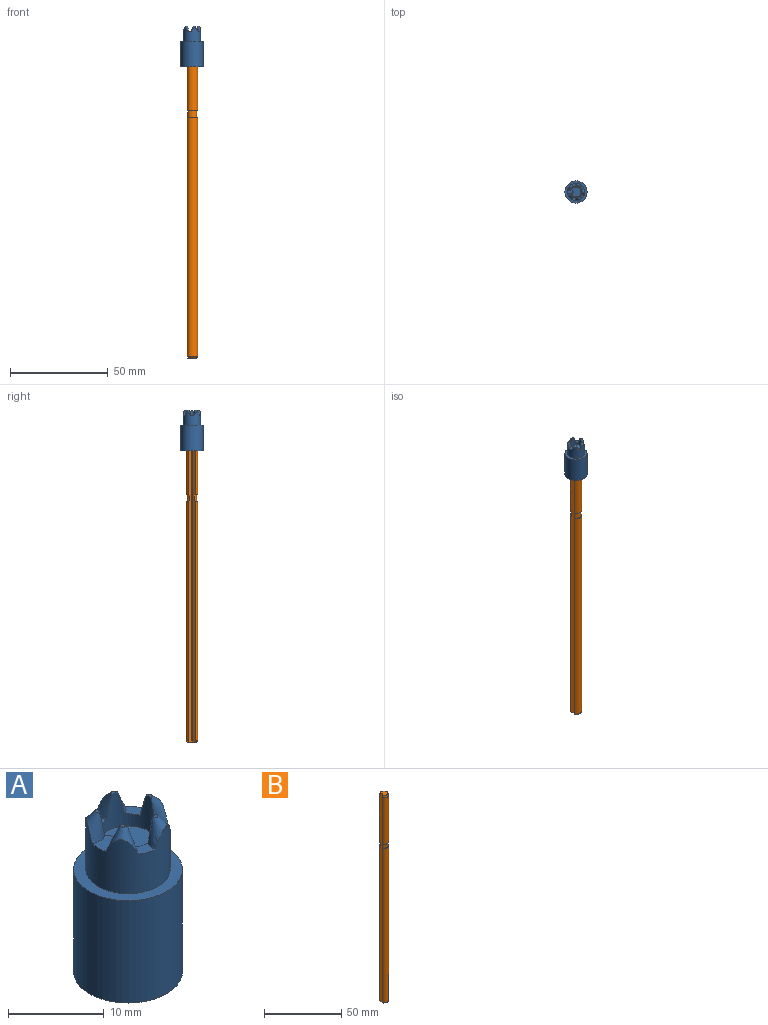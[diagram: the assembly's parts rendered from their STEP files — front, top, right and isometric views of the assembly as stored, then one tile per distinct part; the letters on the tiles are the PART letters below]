
ASSEMBLY  parts=2 mates=1
PART A: 33 faces, bbox 11.7x11.7x21.3 mm
  f0: cylinder r=3.06mm len=6.12mm, axis (0,0,-1), area 44.5mm2, adj f1,f4,f6,f7,f10,f11,f12,f13
  f1: cylinder r=0.15mm len=4.37mm, axis (0,0,-1), area 0.8mm2, adj f0,f2,f17,f32
  f2: plane 3.77x0.68mm, normal (0.71,0.71,0), area 1.9mm2, adj f1,f5,f17,f18,f32
  f3: plane 3.77x0.68mm, normal (0.71,-0.71,0), area 1.9mm2, adj f4,f5,f18,f22,f32
  f4: cylinder r=0.15mm len=4.37mm, axis (0,0,-1), area 0.8mm2, adj f0,f3,f22,f32
  f5: cylinder r=0.9mm len=1.57mm, axis (0,0,-1), area 2.2mm2, adj f2,f3,f18,f32
  f6: cone r=1.8mm half-angle=24.8deg, axis (0.34,0,-0.94), area 9mm2, adj f0,f7,f9,f10,f27
  f7: plane 0.97x0.71mm, normal (0,0,1), area 0.2mm2, adj f0,f6
  f8: cylinder r=3.06mm len=15.9mm, axis (0,0,-1), area 255.9mm2, adj f15,f21,f29,f31
  f9: cylinder r=4.4mm len=8.8mm, axis (0,0,-1), area 159.2mm2, adj f6,f10,f12,f13,f17,f18,f22,f23
  f10: plane 2.32x2.22mm, normal (0,0,1), area 2.2mm2, adj f0,f6,f9,f12
  f11: plane 0.97x0.81mm, normal (0,0,1), area 0.2mm2, adj f0,f12
  f12: cone r=1.8mm half-angle=24.8deg, axis (0.11,0.33,-0.94), area 9mm2, adj f0,f9,f10,f11,f13
  f13: plane 2.2x1.91mm, normal (0,0,1), area 2.2mm2, adj f0,f9,f12,f17
  f14: plane 0.63x0.58mm, normal (0,0,1), area 0.2mm2, adj f0,f17
  f15: cylinder r=0.15mm len=15.9mm, axis (0,0,-1), area 3.1mm2, adj f8,f16,f29,f31
  f16: plane 15.9x0.68mm, normal (0.71,0.71,0), area 15.3mm2, adj f15,f26,f29,f31
  f17: cone r=1.8mm half-angle=24.8deg, axis (-0.28,0.2,-0.94), area 9.8mm2, adj f0,f1,f2,f9,f13,f14,f18
  f18: plane 2.7x2.17mm, normal (0,0,1), area 4.4mm2, adj f2,f3,f5,f9,f17,f22
  f19: plane 0.63x0.58mm, normal (0,0,1), area 0.2mm2, adj f0,f22
  f20: plane 15.9x0.68mm, normal (0.71,-0.71,0), area 15.3mm2, adj f21,f26,f29,f31
  f21: cylinder r=0.15mm len=15.9mm, axis (0,0,-1), area 3.1mm2, adj f8,f20,f29,f31
  f22: cone r=1.8mm half-angle=24.8deg, axis (-0.28,-0.2,-0.94), area 9.8mm2, adj f0,f3,f4,f9,f18,f19,f23
  f23: plane 2.2x1.91mm, normal (0,0,1), area 2.2mm2, adj f0,f9,f22,f24
  f24: cone r=1.8mm half-angle=24.8deg, axis (0.11,-0.33,-0.94), area 9mm2, adj f0,f9,f23,f25,f27
  f25: plane 0.97x0.81mm, normal (0,0,1), area 0.2mm2, adj f0,f24
  f26: cylinder r=0.9mm len=15.9mm, axis (0,0,-1), area 22.5mm2, adj f16,f20,f29,f31
  f27: plane 2.32x2.22mm, normal (0,0,1), area 2.2mm2, adj f0,f6,f9,f24
  f28: cylinder r=5.68mm len=13.05mm, axis (0,0,1), area 465.3mm2, adj f29,f30
  f29: plane 11.35x11.35mm, normal (0,0,-1), area 74.2mm2, adj f8,f15,f16,f20,f21,f26,f28
  f30: plane 11.35x11.35mm, normal (0,0,1), area 40.4mm2, adj f9,f28
  f31: plane 6.12x5.75mm, normal (0,0,-1), area 27mm2, adj f8,f15,f16,f20,f21,f26
  f32: plane 6.12x5.75mm, normal (0,0,1), area 27mm2, adj f0,f1,f2,f3,f4,f5
PART B: 12 faces, bbox 5.6x5.9x165 mm
  f0: cylinder r=2.95mm len=122.55mm, axis (0,0,-1), area 1867.7mm2, adj f1,f3,f7,f11
  f1: plane 165.02x1.36mm, normal (-0.71,0.71,0), area 309.7mm2, adj f0,f2,f4,f5,f6,f7,f8,f9
  f2: cylinder r=2.95mm len=37.05mm, axis (0,0,-1), area 564.7mm2, adj f1,f3,f8,f10
  f3: plane 165.02x1.36mm, normal (-0.71,-0.71,0), area 309.7mm2, adj f0,f2,f4,f5,f6,f7,f8,f9
  f4: cylinder r=0.3mm len=165mm, axis (0,0,-1), area 77.8mm2, adj f1,f3,f5,f6
  f5: plane 5.09x4.75mm, normal (0,0,1), area 18.2mm2, adj f1,f3,f4,f8
  f6: plane 4.69x4.41mm, normal (0,0,-1), area 15.6mm2, adj f1,f3,f4,f7
  f7: cone r=2.95mm half-angle=45deg, axis (0,0,1), area 11.7mm2, adj f0,f1,f3,f6
  f8: cone r=2.54mm half-angle=15deg, axis (0,0,-1), area 22.2mm2, adj f1,f2,f3,f5
  f9: cylinder r=2.4mm len=4.8mm, axis (0,0,-1), area 41.8mm2, adj f1,f3,f10,f11
  f10: plane 5.89x5.45mm, normal (0,0,-1), area 7.6mm2, adj f1,f2,f3,f9
  f11: plane 5.89x5.45mm, normal (0,0,1), area 7.6mm2, adj f0,f1,f3,f9
PLACE A at identity fixed
PLACE B t=(0,0,-162.15)mm
MATE fastened B.f0 <-> A.f0  axis (0,0,1) through (0,0,2.85)mm
